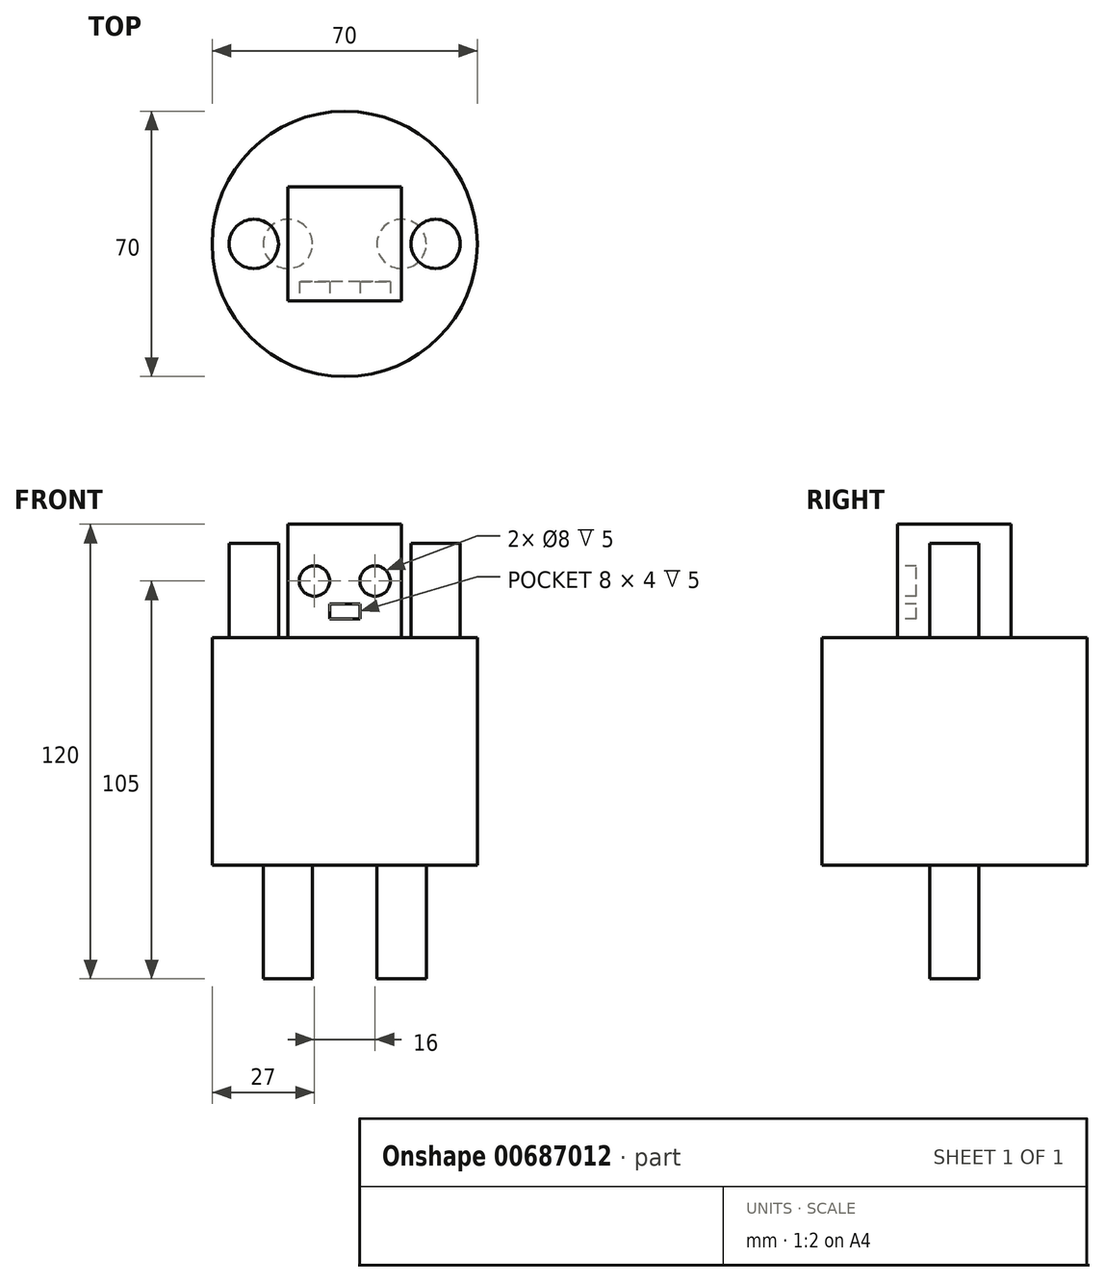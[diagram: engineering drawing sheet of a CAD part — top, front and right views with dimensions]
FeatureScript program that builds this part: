
annotation { "Feature Type Name" : "Feature", "Feature Type Description" : "" }
export const myFeature = defineFeature(function(context is Context, id is Id, definition is map)
    precondition{}
    {
        {
            var Q0;
            Q0=qCreatedBy(makeId("Front.planeOp"),FACE);
            var sketch = newSketch(context, id + "F0", { "sketchPlane" : qUnion([Q0])});
            skLineSegment(sketch, "E0.bottom", {"start": v(15, 25) * mm, "end": v(-15, 25) * mm});
            skLineSegment(sketch, "E0.top", {"start": v(15, 55) * mm, "end": v(-15, 55) * mm});
            skLineSegment(sketch, "E0.left", {"start": v(15, 25) * mm, "end": v(15, 55) * mm});
            skLineSegment(sketch, "E0.right", {"start": v(-15, 25) * mm, "end": v(-15, 55) * mm});
            skPoint(sketch, "E0.middle", {"position": v(0, 40) * mm});
            skSolve(sketch);
        }
        {
            var Q0;
            Q0 = qSketchRegion(id + "F0", true);
            extrude(context, id + "F1", {"entities" : qUnion([Q0]), "endBound" : BoundingType.SYMMETRIC, "depth" : 30 * mm, "offsetDistance" : 25 * mm});
        }
        {
            var Q0;
            Q0=makeQuery(id+"F1.opExtrude","SWEPT_FACE",FACE,{"disambiguationData":[OSD([sQuery(id+"F0.wireOp",EDGE,"E0.bottom")])]});
            var sketch = newSketch(context, id + "F2", { "sketchPlane" : qUnion([Q0])});
            skCircle(sketch, "E1", {"center": v(0, 0) * mm, "radius": 35 * mm});
            skSolve(sketch);
        }
        {
            var Q0;
            Q0 = qSketchRegion(id + "F2", true);
            extrude(context, id + "F3", {"entities" : qUnion([Q0]), "operationType" : NewBodyOperationType.ADD, "depth" : 60 * mm, "offsetDistance" : 25 * mm});
        }
        {
            var Q0;
            Q0=makeQuery(id+"F3.opExtrude","CAP_FACE",FACE,{"disambiguationData":[OSD([sQuery(id+"F2.wireOp",EDGE,"E1")])],"isStart":false});
            var sketch = newSketch(context, id + "F4", { "sketchPlane" : qUnion([Q0])});
            skCircle(sketch, "E2", {"center": v(-15, 0) * mm, "radius": 6.5 * mm});
            skCircle(sketch, "E3", {"center": v(15, 0) * mm, "radius": 6.5 * mm});
            skSolve(sketch);
        }
        {
            var Q0;
            Q0 = qSketchRegion(id + "F4", true);
            extrude(context, id + "F5", {"entities" : qUnion([Q0]), "operationType" : NewBodyOperationType.ADD, "depth" : 30 * mm, "offsetDistance" : 25 * mm});
        }
        {
            var Q0;
            Q0=makeQuery(id+"F1.opExtrude","CAP_FACE",FACE,{"disambiguationData":[OSD([sQuery(id+"F0.wireOp",EDGE,"E0.bottom"),sQuery(id+"F0.wireOp",EDGE,"E0.top"),sQuery(id+"F0.wireOp",EDGE,"E0.left"),sQuery(id+"F0.wireOp",EDGE,"E0.right")])],"isStart":false});
            var sketch = newSketch(context, id + "F6", { "sketchPlane" : qUnion([Q0])});
            skCircle(sketch, "E4", {"center": v(-8, 40) * mm, "radius": 4 * mm});
            skCircle(sketch, "E5", {"center": v(8, 40) * mm, "radius": 4 * mm});
            skLineSegment(sketch, "E6.bottom", {"start": v(4, 30) * mm, "end": v(-4, 30) * mm});
            skLineSegment(sketch, "E6.top", {"start": v(4, 34) * mm, "end": v(-4, 34) * mm});
            skLineSegment(sketch, "E6.left", {"start": v(4, 30) * mm, "end": v(4, 34) * mm});
            skLineSegment(sketch, "E6.right", {"start": v(-4, 30) * mm, "end": v(-4, 34) * mm});
            skPoint(sketch, "E6.middle", {"position": v(0, 32) * mm});
            skSolve(sketch);
        }
        {
            var Q0;
            Q0 = qSketchRegion(id + "F6", true);
            extrude(context, id + "F7", {"entities" : qUnion([Q0]), "operationType" : NewBodyOperationType.REMOVE, "oppositeDirection" : true, "depth" : 5 * mm, "offsetDistance" : 25 * mm});
        }
        {
            var Q0;
            Q0=makeQuery(id+"F3.opExtrude","CAP_FACE",FACE,{"disambiguationData":[OSD([sQuery(id+"F2.wireOp",EDGE,"E1")])],"isStart":true});
            var sketch = newSketch(context, id + "F8", { "sketchPlane" : qUnion([Q0])});
            skCircle(sketch, "E7", {"center": v(-24, 0) * mm, "radius": 6.5 * mm});
            skCircle(sketch, "E8", {"center": v(24, 0) * mm, "radius": 6.5 * mm});
            skSolve(sketch);
        }
        {
            var Q0;
            Q0 = qSketchRegion(id + "F8", true);
            extrude(context, id + "F9", {"entities" : qUnion([Q0]), "operationType" : NewBodyOperationType.ADD, "depth" : 25 * mm, "offsetDistance" : 25 * mm});
        }
    });
